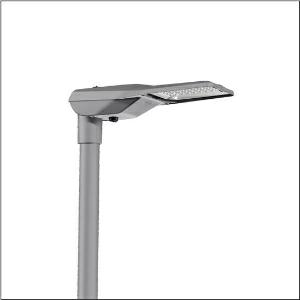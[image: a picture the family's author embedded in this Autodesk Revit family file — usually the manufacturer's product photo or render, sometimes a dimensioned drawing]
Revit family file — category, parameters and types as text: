
# Revit family: streetlight_sl_21_iq_mini___st1_0a_5xe2d21y08hb_5d36
name_source: partatom
category: Lighting Fixtures
units: mm (PartAtom-declared; Revit-internal decimal feet)

## family parameters
Cut with Voids When Loaded = No
Host = Face
Light Source = No
Part Type = Normal
Room Calculation Point = No
Round Connector Dimension = Use Diameter
Shared = No

## types (1)
- --- (1 x LED, 7820 lm, 71 W, 2200K)
    Apparent Load = 71 VA
    CIE Flux Codes = 37 72 97 100 100
    Color Rendering = 70
    Color Temperature = 2200K
    Default Elevation = 1800 mm
    Description = Streetlight SL 21 iQ mini, mast luminaire, primary light control with lens, of PMMA, primary optical cover: cover, of toughened safety glass, transparent, light distribution: ST1.0a, light emission: direct distribution, primary light characteristic: asymmetric, installation type: post-top, side-entry, LED, High Power LED, rated luminous flux: 7.820lm, luminous efficacy: 110lm/W, light colour: 722, colour temperature: 2200K, control: presetting dimming logarithmic, Street-Remote, Auto-Match, Temp-Guard, Lumen-Switch, Night-Set, Smart-Wire, Light-Fading, Desk-Remote (wireless, voltage-free reading and setting of iQ features in the workshop via application-optimized NFC function/RFID function), optimised constant luminous flux control (CLO 2.0), mains connection: 220..240V, AC, 50/60Hz, start of lifetime: 71W, end of service life: 75W, reduction: 30W, luminaire housing, of diecast aluminium, powder-coated, Siteco® metallic grey (DB 702S), corrosivity category C5 mid according to DIN EN ISO 12944, please order mast flange separately, inclination adjustable: 0°, 5°, 10°, 15°, sealing non-destructively replaceable, multi-level sealing system, length: 628mm, width: 235mm, height: 110mm, mast flange for spigot size: 42mm (side-entry): 5XC10008XM4, 60/48mm (side-entry/post-top): 5XC10108XM2, 76/60mm (side-entry/post-top): 5XC10108XM1, Smart Interface below and above, protection rating (complete): IP66, insulation class (complete): insulation class II (safety insulation), certification: CE, ENEC, ENEC+, VDE, impact resistance: IK09, permissible operating ambient temperature for outdoor applications: -40..+50°C, standard-compliant lighting for roads and squares, packaging unit: 1 piece

Light Distribution: ST1.0a
    Height = 110 mm
    Lamp = 1 x LED
    Lamp Light Flux = 7820 lm
    Lamp Power = 71 W
    Lamp count = 1
    Length = 625 mm
    Luminous efficacy = 110 lm/W
    Manufacturer = Siteco
    ModVariant = No
    Model = 5XE2D21Y08HB
    Number of Poles = 1
    OnlyDefault = Yes
    Power Factor = 1
    Product Name = Streetlight SL 21 iQ mini | ST1.0a
    Product group = mast luminaire | pylon top
    ProductGroupID = 6100
    Protection Class = Protection class II
    Protection Degree = IP 66
    RLX_Detail_Level = 1
    RLX_Emergency_Light_Flux = 0 lm
    RLX_Emergency_Type = 0
    RLX_Emergency_Type_DB = No
    RlxData = <blob elided: 92901 chars, md5=02e1a82a>
    Socket = socket
    Standby Power = 0 W
    System Light Flux = 7820 lm
    System Power = 71 W
    Type Comments = factory setting: luminous flux: 100 % | dim-lin: 254 | 716 mA
    Type Image = l_1003514.jpg
    URL = http://relux.com
    VarID = @adj_063229
    Voltage = 0 V
    Weight = 0.00 kg
    Width = 234 mm

## geometry (parser evidence)
native form markers: Blend x4, Sweep x13
no freeform markers — native parametric forms only
